# Revit family: Rack-Q-SYS-QIO Series
name_source: partatom
category: Furniture
units: mm (PartAtom-declared; Revit-internal decimal feet)

## family parameters
Cut with Voids When Loaded = No
Host = Face
OmniClass Number = 23.40.20.27.17
OmniClass Title = Racking
Room Calculation Point = No
Shared = No

## types (1)
- 19" W x 10" D x 2" H
    Body Material = Paint - Q-SYS - Black Matte
    Cost MSRP = 0 $
    Cost Project = 0 $
    Default Elevation = 48 "
    Depth = 10.31 "
    Description = Rack kit for QIO Series.
    Height = 1.72 "
    Manufacturer = Q-SYS
    Manufacturer URL = www.qsys.com
    Model = QIO RMK Rack Kit
    OmniClass Number = 23.40.20.27.17
    Product Documentation Link = https://www.qsys.com
    Product Page URL = https://www.qsys.com
    Regulatory Compliance = Rack
    Type Comments = 19" W x 10" D x 2" H
    URL = https://www.qsys.com
    Weight = 2.40 lbm
    Weight Dimensional = 2.4
    Weight Product = 2.4
    Width = 18.97 "

## geometry (parser evidence)
native form markers: Sweep x2
no freeform markers — native parametric forms only
